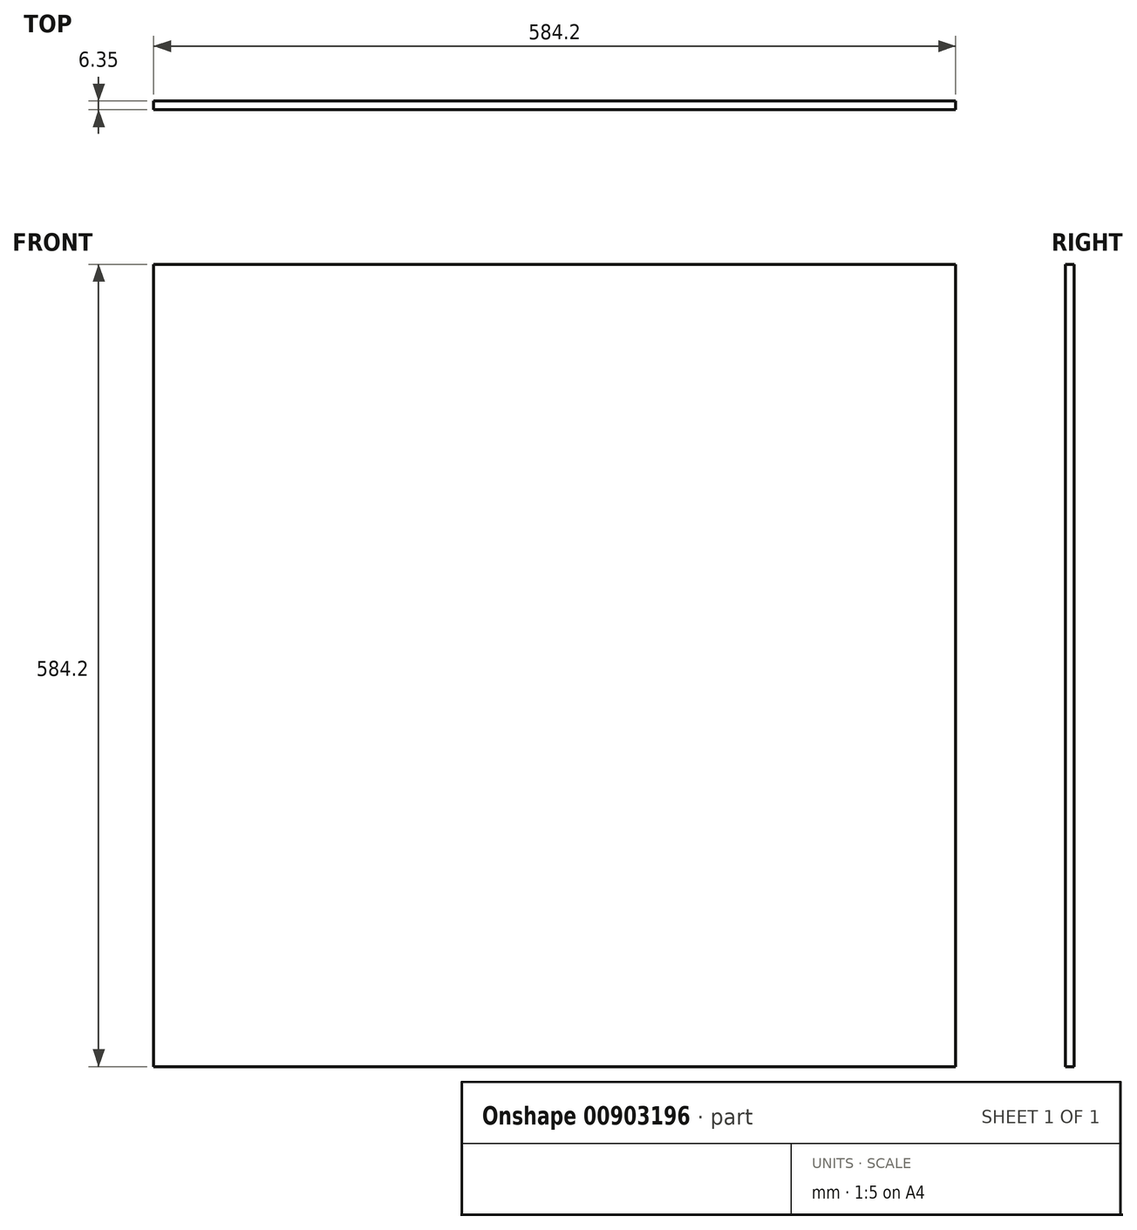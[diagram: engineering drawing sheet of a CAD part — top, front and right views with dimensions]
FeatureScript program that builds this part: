
annotation { "Feature Type Name" : "Feature", "Feature Type Description" : "" }
export const myFeature = defineFeature(function(context is Context, id is Id, definition is map)
    precondition{}
    {
        {
            var Q0;
            Q0=qCreatedBy(makeId("Front.planeOp"),FACE);
            var sketch = newSketch(context, id + "F0", { "sketchPlane" : qUnion([Q0])});
            skLineSegment(sketch, "E0.bottom", {"start": v(292.1, 292.1) * mm, "end": v(-292.1, 292.1) * mm});
            skLineSegment(sketch, "E0.top", {"start": v(292.1, -292.1) * mm, "end": v(-292.1, -292.1) * mm});
            skLineSegment(sketch, "E0.left", {"start": v(292.1, 292.1) * mm, "end": v(292.1, -292.1) * mm});
            skLineSegment(sketch, "E0.right", {"start": v(-292.1, 292.1) * mm, "end": v(-292.1, -292.1) * mm});
            skPoint(sketch, "E0.middle", {"position": v(0, 0) * mm});
            skSolve(sketch);
        }
        {
            var Q0;
            Q0 = qSketchRegion(id + "F0", true);
            extrude(context, id + "F1", {"entities" : qUnion([Q0]), "depth" : 6.35 * mm, "offsetDistance" : 25.4 * mm});
        }
    });
